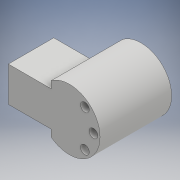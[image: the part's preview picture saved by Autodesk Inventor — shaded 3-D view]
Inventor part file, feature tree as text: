
AUTODESK INVENTOR PART (.ipt)
format: ipt  version: 2018 (Build 220112000, 112)  size: 236,032 bytes
history: native  units: mm
features: extrude x9, sketch x9, other x1
ambient origin geometry x8: Origin, YZ Plane, XZ Plane, XY Plane, X Axis, Y Axis, Z Axis, Center Point
bodies: Body1 (feature_tree)
feature tree (19):
  other  "Sólido1"
  extrude  "Extrusión1"  Depth=18.0mm TaperAngle=0.0deg
  extrude  "Extrusión2"  Depth=3.0mm
  extrude  "Extrusión3"  Depth=23.0mm TaperAngle=0.0deg
  extrude  "Extrusión4"  Depth=15.0mm TaperAngle=0.0deg
  extrude  "Extrusión5"  Depth=20.0mm
  extrude  "Extrusión6"  TaperAngle=45.0deg  [1 undecoded]
  extrude  "Extrusión7"  TaperAngle=45.0deg  [1 undecoded]
  extrude  "Extrusión8"  Depth=15.0mm TaperAngle=0.0deg
  extrude  "Extrusión9"  Depth=26.0mm TaperAngle=0.0deg
  sketch  "Boceto1"  dims[d3=6.0mm d5=5.0mm d6=14.0mm d7=2.0mm d8=14.0mm d9=90.0deg d10=19.0mm d11=5.0mm d12=180.0deg d13=14.0mm d14=2.0mm d18=18.0mm d19=0.0mm]
  sketch  "Boceto2"  dims[d21=3.0mm d22=3.0mm]
  sketch  "Boceto3"  dims[d23=3.0mm d24=23.0mm d25=0.0mm]
  sketch  "Boceto4"  dims[d26=3.0mm d27=0.0mm d30=15.0mm d31=0.0mm]
  sketch  "Boceto5"  dims[d32=20.0mm d33=35.0mm]
  sketch  "Boceto6"  dims[d35=4.0mm d36=45.0deg]
  sketch  "Boceto7"  dims[d37=4.0mm d38=45.0deg]
  sketch  "Boceto8"  dims[d39=15.0mm d40=0.0mm d41=15.0mm d42=0.0mm]
  sketch  "Boceto9"  dims[d43=20.0mm d44=26.0mm d45=0.0mm d46=13.75mm d47=13.75mm d48=8.726646mm d49=13.75mm d50=8.726646mm d51=3.5mm d52=3.5mm d53=3.5mm d54=41.0mm d55=0.0mm d56=5.0mm d57=5.0mm d58=5.0mm d59=36.0mm d60=0.0mm]
note: 2 required parameter values undecoded (feature->parameter linkage not recoverable at this tier; creation-order binding heuristic only, values carry confidence <= 0.55)
